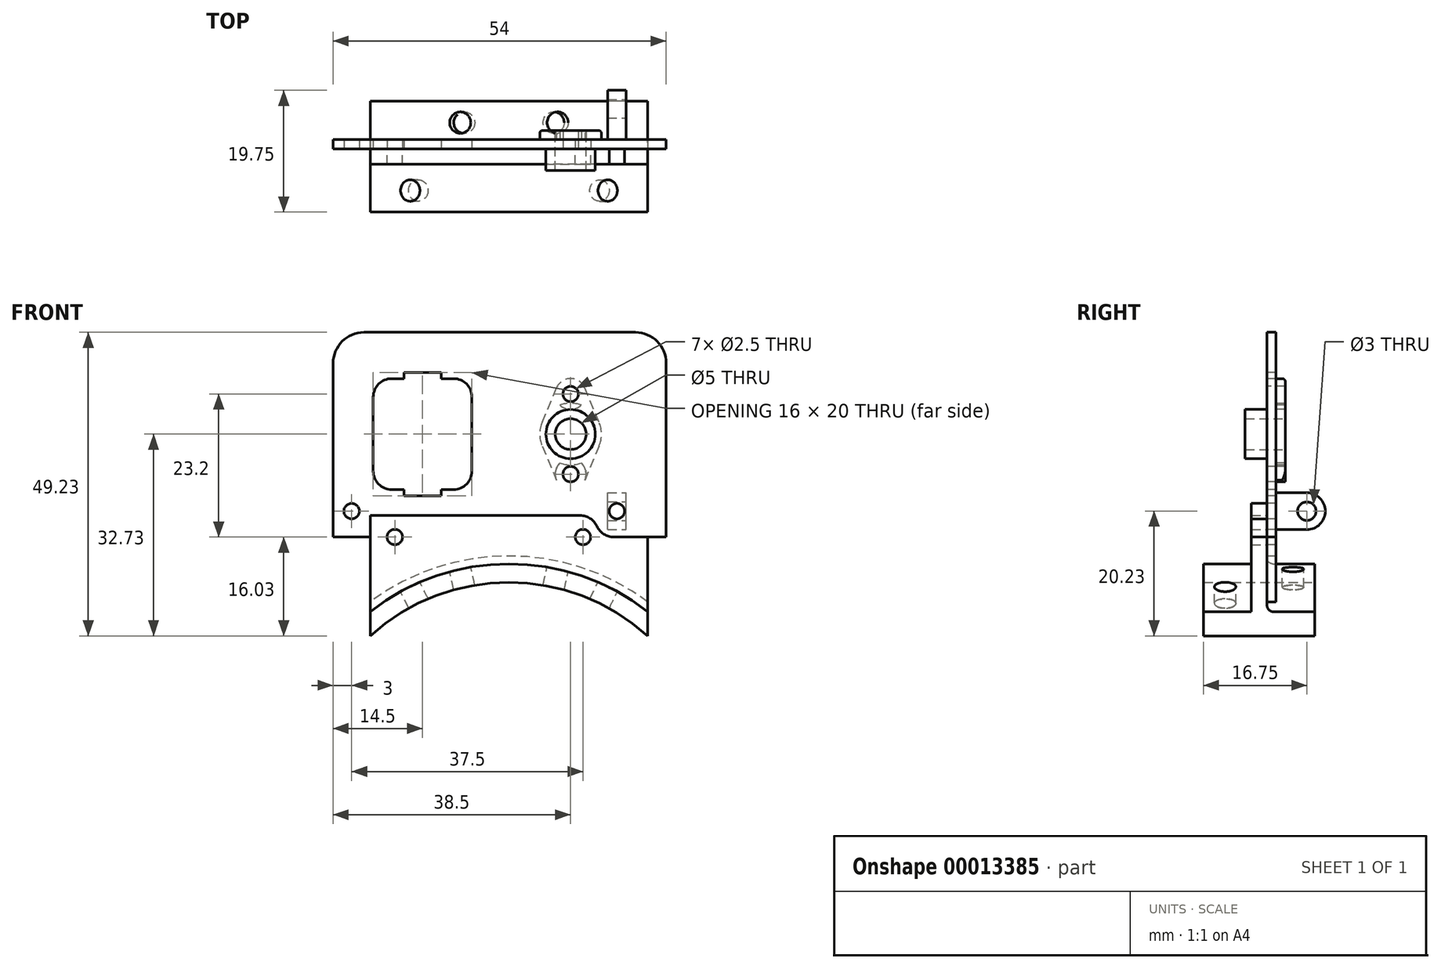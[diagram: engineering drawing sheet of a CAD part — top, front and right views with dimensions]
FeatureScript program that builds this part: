
annotation { "Feature Type Name" : "Feature", "Feature Type Description" : "" }
export const myFeature = defineFeature(function(context is Context, id is Id, definition is map)
    precondition{}
    {
        {
            var Q0;
            Q0=qCreatedBy(makeId("Front.planeOp"),FACE);
            var sketch = newSketch(context, id + "F0", { "sketchPlane" : qUnion([Q0])});
            skCircle(sketch, "E0", {"center": v(0, 0) * mm, "radius": 33.5 * mm});
            skCircle(sketch, "E1", {"center": v(0, 0) * mm, "radius": 36.5 * mm});
            skLineSegment(sketch, "E2", {"start": v(0, 0) * mm, "end": v(0, 40.85) * mm, "construction": true});
            skLineSegment(sketch, "E3", {"start": v(0, 40.85) * mm, "end": v(-22.5, 40.85) * mm, "construction": true});
            skLineSegment(sketch, "E4", {"start": v(0, 40.85) * mm, "end": v(12, 40.85) * mm, "construction": true});
            skCircle(sketch, "E5", {"center": v(-18.5, 40.85) * mm, "radius": 1.25 * mm});
            skCircle(sketch, "E6", {"center": v(12, 40.85) * mm, "radius": 1.25 * mm});
            skLineSegment(sketch, "E7.0", {"start": v(22.5, 0) * mm, "end": v(22.5, 40.85) * mm, "construction": true});
            skLineSegment(sketch, "E8.0.MirrorCS", {"start": v(-22.5, 0) * mm, "end": v(-22.5, 40.85) * mm, "construction": true});
            skLineSegment(sketch, "E9.0", {"start": v(0, 44.35) * mm, "end": v(-22.5, 44.35) * mm});
            skLineSegment(sketch, "E10", {"start": v(-22.5, 44.35) * mm, "end": v(-22.5, 24.82) * mm});
            skLineSegment(sketch, "E11", {"start": v(0, 44.35) * mm, "end": v(22.5, 44.35) * mm});
            skLineSegment(sketch, "E12", {"start": v(22.5, 44.35) * mm, "end": v(22.5, 24.82) * mm});
            skLineSegment(sketch, "E13", {"start": v(22.5, 40.85) * mm, "end": v(17, 40.85) * mm});
            skLineSegment(sketch, "E14.bottom", {"start": v(17, 40.85) * mm, "end": v(12, 40.85) * mm});
            skLineSegment(sketch, "E14.top", {"start": v(17, 44.35) * mm, "end": v(12, 44.35) * mm});
            skLineSegment(sketch, "E14.left", {"start": v(17, 40.85) * mm, "end": v(17, 44.35) * mm});
            skLineSegment(sketch, "E14.right", {"start": v(12, 40.85) * mm, "end": v(12, 44.35) * mm});
            skCircle(sketch, "E15", {"center": v(12, 44.35) * mm, "radius": 3 * mm, "construction": true});
            skCircle(sketch, "E16", {"center": v(17, 40.85) * mm, "radius": 3 * mm, "construction": true});
            skLineSegment(sketch, "E17", {"start": v(12, 41.35) * mm, "end": v(14.04, 41.35) * mm, "construction": true});
            skLineSegment(sketch, "E18", {"start": v(17, 43.85) * mm, "end": v(14.96, 43.85) * mm, "construction": true});
            skCircle(sketch, "E19", {"center": v(17, 43.85) * mm, "radius": 3 * mm});
            skLineSegment(sketch, "E20", {"start": v(12, 41.35) * mm, "end": v(7.9, 41.35) * mm, "construction": true});
            skCircle(sketch, "E21", {"center": v(17, 43.85) * mm, "radius": 6 * mm, "construction": true});
            skCircle(sketch, "E22", {"center": v(11.55, 41.35) * mm, "radius": 3 * mm});
            skSolve(sketch);
        }
        {
            var Q0;
            {var subQ3=sQuery(id+"F0.wireOp",EDGE,"E0");var subQ5=sQuery(id+"F0.wireOp",EDGE,"E10");var subQ7=makeQuery(id+"F0.imprint","INTERSECT",VERTEX,{"derivedFrom":[subQ3,subQ5]});Q0=makeQuery(id+"F0.imprint","IMPRINT",FACE,{"disambiguationData":[TD([[makeQuery(id+"F0.imprint","IMPRINT",EDGE,{"disambiguationData":[TD([[subQ7,1.0]])],"derivedFrom":subQ3}),-1.0]])]});}
            extrude(context, id + "F1", {"entities" : qUnion([Q0]), "endBound" : BoundingType.SYMMETRIC, "depth" : 18 * mm});
        }
        {
            var Q0;
            Q0=makeQuery(id+"F0.imprint","IMPRINT",FACE,{"disambiguationData":[TD([[makeQuery(id+"F0.imprint","IMPRINT",EDGE,{"derivedFrom":sQuery(id+"F0.wireOp",EDGE,"E5")}),-1.0]])]});
            var Q1;
            {var subQ1=sQuery(id+"F0.wireOp",EDGE,"E14.bottom");var subQ6=sQuery(id+"F0.wireOp",EDGE,"E6");var subQ8=makeQuery(id+"F0.imprint","INTERSECT",VERTEX,{"derivedFrom":[subQ6,subQ1]});Q1=makeQuery(id+"F0.imprint","IMPRINT",FACE,{"disambiguationData":[TD([[makeQuery(id+"F0.imprint","IMPRINT",EDGE,{"disambiguationData":[TD([[subQ8,1.0]])],"derivedFrom":subQ6}),-1.0]])]});}
            var Q2;
            {var subQ0=sQuery(id+"F0.wireOp",EDGE,"E22");var subQ3=sQuery(id+"F0.wireOp",EDGE,"E14.bottom");var subQ4=makeQuery(id+"F0.imprint","INTERSECT",VERTEX,{"derivedFrom":[subQ3,subQ0]});Q2=makeQuery(id+"F0.imprint","IMPRINT",FACE,{"disambiguationData":[TD([[makeQuery(id+"F0.imprint","IMPRINT",EDGE,{"disambiguationData":[TD([[subQ4,-1.0]])],"derivedFrom":subQ0}),-1.0]])]});}
            var Q3;
            {var subQ2=sQuery(id+"F0.wireOp",EDGE,"E14.bottom");var subQ6=sQuery(id+"F0.wireOp",EDGE,"E6");var subQ8=makeQuery(id+"F0.imprint","INTERSECT",VERTEX,{"derivedFrom":[subQ6,subQ2]});Q3=makeQuery(id+"F0.imprint","IMPRINT",FACE,{"disambiguationData":[TD([[makeQuery(id+"F0.imprint","IMPRINT",EDGE,{"disambiguationData":[TD([[subQ8,-1.0]])],"derivedFrom":subQ6}),-1.0]])]});}
            extrude(context, id + "F2", {"entities" : qUnion([Q0, Q1, Q2, Q3]), "operationType" : NewBodyOperationType.ADD, "endBound" : BoundingType.SYMMETRIC, "depth" : 2.5 * mm});
        }
        {
            var Q0;
            Q0=makeQuery(id+"F2.opExtrude","CAP_FACE",FACE,{"disambiguationData":[OSD([sQuery(id+"F0.wireOp",EDGE,"E1"),sQuery(id+"F0.wireOp",EDGE,"E5"),sQuery(id+"F0.wireOp",EDGE,"E6"),sQuery(id+"F0.wireOp",EDGE,"E10"),sQuery(id+"F0.wireOp",EDGE,"E11"),sQuery(id+"F0.wireOp",EDGE,"E12"),sQuery(id+"F0.wireOp",EDGE,"E13"),sQuery(id+"F0.wireOp",EDGE,"E19"),sQuery(id+"F0.wireOp",EDGE,"E22")])],"isStart":true});
            var sketch = newSketch(context, id + "F3", { "sketchPlane" : qUnion([Q0])});
            skLineSegment(sketch, "E23.0", {"start": v(0, 0) * mm, "end": v(0, 40.85) * mm, "construction": true});
            skCircle(sketch, "E23.1", {"center": v(-12, 40.85) * mm, "radius": 1.25 * mm});
            skCircle(sketch, "E23.2", {"center": v(18.5, 40.85) * mm, "radius": 1.25 * mm});
            skLineSegment(sketch, "E24", {"start": v(0, 40.85) * mm, "end": v(-22.5, 40.85) * mm, "construction": true});
            skLineSegment(sketch, "E25", {"start": v(0, 40.85) * mm, "end": v(22.5, 40.85) * mm, "construction": true});
            skLineSegment(sketch, "E26", {"start": v(-22.5, 40.85) * mm, "end": v(-22.5, 30.35) * mm});
            skLineSegment(sketch, "E27", {"start": v(-22.5, 30.35) * mm, "end": v(22.5, 30.35) * mm});
            skLineSegment(sketch, "E28", {"start": v(22.5, 30.35) * mm, "end": v(22.5, 40.85) * mm});
            skCircle(sketch, "E29", {"center": v(0, 0) * mm, "radius": 37.78 * mm});
            skLineSegment(sketch, "E30.bottom", {"start": v(-22.5, 40.85) * mm, "end": v(-25.5, 40.85) * mm});
            skLineSegment(sketch, "E30.top", {"start": v(-20.5, 74.05) * mm, "end": v(-22.5, 74.05) * mm});
            skLineSegment(sketch, "E30.left", {"start": v(-22.5, 40.85) * mm, "end": v(-22.5, 74.05) * mm});
            skLineSegment(sketch, "E30.right", {"start": v(-25.5, 40.85) * mm, "end": v(-25.5, 69.05) * mm});
            skLineSegment(sketch, "E31.bottom", {"start": v(22.5, 40.85) * mm, "end": v(28.5, 40.85) * mm});
            skLineSegment(sketch, "E31.top", {"start": v(22.5, 74.05) * mm, "end": v(23.5, 74.05) * mm});
            skLineSegment(sketch, "E31.left", {"start": v(22.5, 40.85) * mm, "end": v(22.5, 74.05) * mm});
            skLineSegment(sketch, "E31.right", {"start": v(28.5, 40.85) * mm, "end": v(28.5, 69.05) * mm});
            skLineSegment(sketch, "E32", {"start": v(-22.5, 74.05) * mm, "end": v(22.5, 74.05) * mm});
            skPoint(sketch, "E33.visualSharp", {"position": v(-25.5, 74.05) * mm});
            skArc(sketch, "E33.filletArc", {"start": v(-20.5, 74.05) * mm, "mid": v(-24.04, 72.59) * mm, "end": v(-25.5, 69.05) * mm});
            skPoint(sketch, "E34.visualSharp", {"position": v(28.5, 74.05) * mm});
            skArc(sketch, "E34.filletArc", {"start": v(28.5, 69.05) * mm, "mid": v(27.04, 72.59) * mm, "end": v(23.5, 74.05) * mm});
            skLineSegment(sketch, "E35", {"start": v(0, 40.85) * mm, "end": v(0, 74.05) * mm, "construction": true});
            skLineSegment(sketch, "E36", {"start": v(-10, 74.05) * mm, "end": v(-10, 40.85) * mm, "construction": true});
            skLineSegment(sketch, "E37", {"start": v(14, 74.05) * mm, "end": v(14, 40.85) * mm, "construction": true});
            skLineSegment(sketch, "E38", {"start": v(-17.5, 74.05) * mm, "end": v(-17.5, 45.05) * mm, "construction": true});
            skLineSegment(sketch, "E39", {"start": v(-17.5, 45.05) * mm, "end": v(25.5, 45.05) * mm, "construction": true});
            skLineSegment(sketch, "E40", {"start": v(-25.5, 57.55) * mm, "end": v(28.5, 57.55) * mm, "construction": true});
            skCircle(sketch, "E41", {"center": v(-10, 57.55) * mm, "radius": 4 * mm});
            skCircle(sketch, "E42", {"center": v(-10, 57.55) * mm, "radius": 6.5 * mm, "construction": true});
            skCircle(sketch, "E43", {"center": v(-17.5, 45.05) * mm, "radius": 1.25 * mm});
            skCircle(sketch, "E44", {"center": v(25.5, 45.05) * mm, "radius": 1.25 * mm});
            skLineSegment(sketch, "E45.rect.bottom", {"start": v(17, 47.55) * mm, "end": v(11, 47.55) * mm});
            skLineSegment(sketch, "E45.rect.top", {"start": v(17, 67.55) * mm, "end": v(11, 67.55) * mm});
            skLineSegment(sketch, "E45.rect.left", {"start": v(17, 47.55) * mm, "end": v(17, 67.55) * mm});
            skLineSegment(sketch, "E45.rect.right", {"start": v(11, 47.55) * mm, "end": v(11, 67.55) * mm});
            skPoint(sketch, "E45.rect.middle", {"position": v(14, 57.55) * mm});
            skLineSegment(sketch, "E46.rect.bottom", {"start": v(19, 48.55) * mm, "end": v(9, 48.55) * mm});
            skLineSegment(sketch, "E46.rect.top", {"start": v(19, 66.55) * mm, "end": v(9, 66.55) * mm});
            skLineSegment(sketch, "E46.rect.left", {"start": v(22, 51.55) * mm, "end": v(22, 63.55) * mm});
            skLineSegment(sketch, "E46.rect.right", {"start": v(6, 51.55) * mm, "end": v(6, 63.55) * mm});
            skPoint(sketch, "E47.visualSharp", {"position": v(6, 66.55) * mm});
            skArc(sketch, "E47.filletArc", {"start": v(9, 66.55) * mm, "mid": v(6.88, 65.67) * mm, "end": v(6, 63.55) * mm});
            skPoint(sketch, "E48.visualSharp", {"position": v(6, 48.55) * mm});
            skArc(sketch, "E48.filletArc", {"start": v(6, 51.55) * mm, "mid": v(6.88, 49.43) * mm, "end": v(9, 48.55) * mm});
            skPoint(sketch, "E49.visualSharp", {"position": v(22, 48.55) * mm});
            skArc(sketch, "E49.filletArc", {"start": v(19, 48.55) * mm, "mid": v(21.12, 49.43) * mm, "end": v(22, 51.55) * mm});
            skPoint(sketch, "E50.visualSharp", {"position": v(22, 66.55) * mm});
            skArc(sketch, "E50.filletArc", {"start": v(22, 63.55) * mm, "mid": v(21.12, 65.67) * mm, "end": v(19, 66.55) * mm});
            skCircle(sketch, "E51", {"center": v(-10, 64.05) * mm, "radius": 1.25 * mm});
            skCircle(sketch, "E52.0.MirrorC", {"center": v(-10, 51.05) * mm, "radius": 1.25 * mm});
            skSolve(sketch);
        }
        {
            var Q0;
            Q0=makeQuery(id+"F3.imprint","IMPRINT",FACE,{"disambiguationData":[TD([[makeQuery(id+"F3.imprint","IMPRINT",EDGE,{"derivedFrom":sQuery(id+"F3.wireOp",EDGE,"E23.1")}),1.0]])]});
            var Q1;
            Q1=makeQuery(id+"F3.imprint","IMPRINT",FACE,{"disambiguationData":[TD([[makeQuery(id+"F3.imprint","IMPRINT",EDGE,{"derivedFrom":sQuery(id+"F3.wireOp",EDGE,"E41")}),-1.0]])]});
            var Q2;
            {var subQ4=sQuery(id+"F3.wireOp",EDGE,"E30.bottom");Q2=makeQuery(id+"F3.imprint","IMPRINT",FACE,{"disambiguationData":[TD([[makeQuery(id+"F3.imprint","IMPRINT",EDGE,{"derivedFrom":subQ4}),-1.0]])]});}
            var Q3;
            {var subQ3=sQuery(id+"F3.wireOp",EDGE,"E31.bottom");Q3=makeQuery(id+"F3.imprint","IMPRINT",FACE,{"disambiguationData":[TD([[makeQuery(id+"F3.imprint","IMPRINT",EDGE,{"derivedFrom":subQ3}),1.0]])]});}
            extrude(context, id + "F4", {"entities" : qUnion([Q0, Q1, Q2, Q3]), "depth" : 1.5 * mm});
        }
        {
            var Q0;
            Q0=makeQuery(id+"F2.opExtrude","CAP_EDGE",EDGE,{"disambiguationData":[OSD([sQuery(id+"F0.wireOp",EDGE,"E1")])],"isStart":false});
            var Q1;
            Q1=makeQuery(id+"F2.opExtrude","CAP_EDGE",EDGE,{"disambiguationData":[OSD([sQuery(id+"F0.wireOp",EDGE,"E1")])],"isStart":true});
            fillet(context, id + "F5", {"entities" : qUnion([Q0, Q1]), "radius" : 1 * mm, "tangentPropagation" : true, "allowEdgeOverflow" : false});
        }
        {
            var Q0;
            Q0=makeQuery(id+"F4.opExtrude","CAP_FACE",FACE,{"disambiguationData":[OSD([sQuery(id+"F3.wireOp",EDGE,"E23.1"),sQuery(id+"F3.wireOp",EDGE,"E23.2"),sQuery(id+"F3.wireOp",EDGE,"E26"),sQuery(id+"F3.wireOp",EDGE,"E28"),sQuery(id+"F3.wireOp",EDGE,"E29"),sQuery(id+"F3.wireOp",EDGE,"E30.bottom"),sQuery(id+"F3.wireOp",EDGE,"E30.right"),sQuery(id+"F3.wireOp",EDGE,"E31.bottom"),sQuery(id+"F3.wireOp",EDGE,"E31.top"),sQuery(id+"F3.wireOp",EDGE,"E31.right"),sQuery(id+"F3.wireOp",EDGE,"E32"),sQuery(id+"F3.wireOp",EDGE,"E33.filletArc"),sQuery(id+"F3.wireOp",EDGE,"E34.filletArc"),sQuery(id+"F3.wireOp",EDGE,"E41"),sQuery(id+"F3.wireOp",EDGE,"E43"),sQuery(id+"F3.wireOp",EDGE,"E44"),sQuery(id+"F3.wireOp",EDGE,"E45.rect.bottom"),sQuery(id+"F3.wireOp",EDGE,"E45.rect.top"),sQuery(id+"F3.wireOp",EDGE,"E45.rect.left"),sQuery(id+"F3.wireOp",EDGE,"E45.rect.right"),sQuery(id+"F3.wireOp",EDGE,"E46.rect.bottom"),sQuery(id+"F3.wireOp",EDGE,"E46.rect.top"),sQuery(id+"F3.wireOp",EDGE,"E46.rect.left"),sQuery(id+"F3.wireOp",EDGE,"E46.rect.right"),sQuery(id+"F3.wireOp",EDGE,"E47.filletArc"),sQuery(id+"F3.wireOp",EDGE,"E48.filletArc"),sQuery(id+"F3.wireOp",EDGE,"E49.filletArc"),sQuery(id+"F3.wireOp",EDGE,"E50.filletArc"),sQuery(id+"F3.wireOp",EDGE,"E51"),sQuery(id+"F3.wireOp",EDGE,"E52.0.MirrorC")])],"isStart":false});
            var sketch = newSketch(context, id + "F6", { "sketchPlane" : qUnion([Q0])});
            skCircle(sketch, "E53.0", {"center": v(-10, 57.55) * mm, "radius": 4 * mm});
            skCircle(sketch, "E53.1", {"center": v(-10, 64.05) * mm, "radius": 1.25 * mm});
            skCircle(sketch, "E53.2", {"center": v(-10, 51.05) * mm, "radius": 1.25 * mm});
            skCircle(sketch, "E54", {"center": v(-10, 57.55) * mm, "radius": 5 * mm});
            skCircle(sketch, "E55", {"center": v(-10, 57.55) * mm, "radius": 2.5 * mm});
            skCircle(sketch, "E56", {"center": v(-10, 64.05) * mm, "radius": 2.5 * mm});
            skCircle(sketch, "E57", {"center": v(-10, 51.05) * mm, "radius": 2.5 * mm});
            skLineSegment(sketch, "E58", {"start": v(-14.62, 55.63) * mm, "end": v(-12.3, 50.09) * mm});
            skLineSegment(sketch, "E59", {"start": v(-5.38, 55.63) * mm, "end": v(-7.7, 50.09) * mm});
            skLineSegment(sketch, "E60", {"start": v(-14.62, 59.47) * mm, "end": v(-12.3, 65.01) * mm});
            skLineSegment(sketch, "E61", {"start": v(-5.38, 59.47) * mm, "end": v(-7.7, 65.01) * mm});
            skSolve(sketch);
        }
        {
            var Q0;
            Q0=makeQuery(id+"F6.imprint","IMPRINT",FACE,{"disambiguationData":[TD([[makeQuery(id+"F6.imprint","IMPRINT",EDGE,{"derivedFrom":sQuery(id+"F6.wireOp",EDGE,"E55")}),-1.0]])]});
            extrude(context, id + "F7", {"entities" : qUnion([Q0]), "oppositeDirection" : true, "depth" : 5 * mm});
        }
        {
            var Q0;
            {var subQ3=sQuery(id+"F6.wireOp",EDGE,"E53.0");var subQ5=sQuery(id+"F6.wireOp",EDGE,"E56");var subQ7=makeQuery(id+"F6.imprint","INTERSECT",VERTEX,{"derivedFrom":[subQ3,subQ5]});Q0=makeQuery(id+"F6.imprint","IMPRINT",FACE,{"disambiguationData":[TD([[makeQuery(id+"F6.imprint","IMPRINT",EDGE,{"disambiguationData":[TD([[subQ7,-1.0]])],"derivedFrom":subQ3}),-1.0]])]});}
            var Q1;
            Q1=makeQuery(id+"F6.imprint","IMPRINT",FACE,{"disambiguationData":[TD([[makeQuery(id+"F6.imprint","IMPRINT",EDGE,{"derivedFrom":sQuery(id+"F6.wireOp",EDGE,"E55")}),-1.0]])]});
            var Q2;
            {var subQ0=sQuery(id+"F6.wireOp",EDGE,"E56");var subQ1=sQuery(id+"F6.wireOp",EDGE,"E54");var subQ2=makeQuery(id+"F6.imprint","INTERSECT",VERTEX,{"disambiguationData":[OD(0.0)],"derivedFrom":[subQ1,subQ0]});Q2=makeQuery(id+"F6.imprint","IMPRINT",FACE,{"disambiguationData":[TD([[makeQuery(id+"F6.imprint","IMPRINT",EDGE,{"disambiguationData":[TD([[subQ2,-1.0]])],"derivedFrom":subQ1}),1.0]])]});}
            var Q3;
            Q3=makeQuery(id+"F6.imprint","IMPRINT",FACE,{"disambiguationData":[TD([[makeQuery(id+"F6.imprint","IMPRINT",EDGE,{"derivedFrom":sQuery(id+"F6.wireOp",EDGE,"E53.1")}),-1.0]])]});
            var Q4;
            {var subQ0=sQuery(id+"F6.wireOp",EDGE,"E60");Q4=makeQuery(id+"F6.imprint","IMPRINT",FACE,{"disambiguationData":[TD([[makeQuery(id+"F6.imprint","IMPRINT",EDGE,{"derivedFrom":subQ0}),-1.0]])]});}
            var Q5;
            {var subQ3=sQuery(id+"F6.wireOp",EDGE,"E53.0");var subQ5=sQuery(id+"F6.wireOp",EDGE,"E56");var subQ7=makeQuery(id+"F6.imprint","INTERSECT",VERTEX,{"derivedFrom":[subQ3,subQ5]});Q5=makeQuery(id+"F6.imprint","IMPRINT",FACE,{"disambiguationData":[TD([[makeQuery(id+"F6.imprint","IMPRINT",EDGE,{"disambiguationData":[TD([[subQ7,1.0]])],"derivedFrom":subQ3}),-1.0]])]});}
            var Q6;
            {var subQ0=sQuery(id+"F6.wireOp",EDGE,"E61");Q6=makeQuery(id+"F6.imprint","IMPRINT",FACE,{"disambiguationData":[TD([[makeQuery(id+"F6.imprint","IMPRINT",EDGE,{"derivedFrom":subQ0}),1.0]])]});}
            var Q7;
            {var subQ0=sQuery(id+"F6.wireOp",EDGE,"E57");var subQ1=sQuery(id+"F6.wireOp",EDGE,"E54");var subQ2=makeQuery(id+"F6.imprint","INTERSECT",VERTEX,{"disambiguationData":[OD(0.0)],"derivedFrom":[subQ1,subQ0]});Q7=makeQuery(id+"F6.imprint","IMPRINT",FACE,{"disambiguationData":[TD([[makeQuery(id+"F6.imprint","IMPRINT",EDGE,{"disambiguationData":[TD([[subQ2,-1.0]])],"derivedFrom":subQ1}),1.0]])]});}
            var Q8;
            Q8=makeQuery(id+"F6.imprint","IMPRINT",FACE,{"disambiguationData":[TD([[makeQuery(id+"F6.imprint","IMPRINT",EDGE,{"derivedFrom":sQuery(id+"F6.wireOp",EDGE,"E53.2")}),1.0]])]});
            var Q9;
            {var subQ0=sQuery(id+"F6.wireOp",EDGE,"E58");Q9=makeQuery(id+"F6.imprint","IMPRINT",FACE,{"disambiguationData":[TD([[makeQuery(id+"F6.imprint","IMPRINT",EDGE,{"derivedFrom":subQ0}),1.0]])]});}
            var Q10;
            {var subQ0=sQuery(id+"F6.wireOp",EDGE,"E59");Q10=makeQuery(id+"F6.imprint","IMPRINT",FACE,{"disambiguationData":[TD([[makeQuery(id+"F6.imprint","IMPRINT",EDGE,{"derivedFrom":subQ0}),-1.0]])]});}
            extrude(context, id + "F8", {"entities" : qUnion([Q0, Q1, Q2, Q3, Q4, Q5, Q6, Q7, Q8, Q9, Q10]), "operationType" : NewBodyOperationType.ADD, "depth" : 1.5 * mm});
        }
        {
            var Q0;
            Q0=makeQuery(id+"F8.opExtrude","CAP_EDGE",EDGE,{"disambiguationData":[OSD([sQuery(id+"F6.wireOp",EDGE,"E60")])],"isStart":false});
            fillet(context, id + "F9", {"entities" : qUnion([Q0]), "radius" : 0.5 * mm, "tangentPropagation" : true, "allowEdgeOverflow" : false});
        }
        {
            var Q0;
            Q0=makeQuery(id+"F4.opExtrude","CAP_FACE",FACE,{"disambiguationData":[OSD([sQuery(id+"F3.wireOp",EDGE,"E23.1"),sQuery(id+"F3.wireOp",EDGE,"E23.2"),sQuery(id+"F3.wireOp",EDGE,"E26"),sQuery(id+"F3.wireOp",EDGE,"E28"),sQuery(id+"F3.wireOp",EDGE,"E29"),sQuery(id+"F3.wireOp",EDGE,"E30.bottom"),sQuery(id+"F3.wireOp",EDGE,"E30.right"),sQuery(id+"F3.wireOp",EDGE,"E31.bottom"),sQuery(id+"F3.wireOp",EDGE,"E31.top"),sQuery(id+"F3.wireOp",EDGE,"E31.right"),sQuery(id+"F3.wireOp",EDGE,"E32"),sQuery(id+"F3.wireOp",EDGE,"E33.filletArc"),sQuery(id+"F3.wireOp",EDGE,"E34.filletArc"),sQuery(id+"F3.wireOp",EDGE,"E41"),sQuery(id+"F3.wireOp",EDGE,"E43"),sQuery(id+"F3.wireOp",EDGE,"E44"),sQuery(id+"F3.wireOp",EDGE,"E45.rect.bottom"),sQuery(id+"F3.wireOp",EDGE,"E45.rect.top"),sQuery(id+"F3.wireOp",EDGE,"E45.rect.left"),sQuery(id+"F3.wireOp",EDGE,"E45.rect.right"),sQuery(id+"F3.wireOp",EDGE,"E46.rect.bottom"),sQuery(id+"F3.wireOp",EDGE,"E46.rect.top"),sQuery(id+"F3.wireOp",EDGE,"E46.rect.left"),sQuery(id+"F3.wireOp",EDGE,"E46.rect.right"),sQuery(id+"F3.wireOp",EDGE,"E47.filletArc"),sQuery(id+"F3.wireOp",EDGE,"E48.filletArc"),sQuery(id+"F3.wireOp",EDGE,"E49.filletArc"),sQuery(id+"F3.wireOp",EDGE,"E50.filletArc"),sQuery(id+"F3.wireOp",EDGE,"E51"),sQuery(id+"F3.wireOp",EDGE,"E52.0.MirrorC")])],"isStart":false});
            var sketch = newSketch(context, id + "F10", { "sketchPlane" : qUnion([Q0])});
            skCircle(sketch, "E62.0", {"center": v(-17.5, 45.05) * mm, "radius": 1.25 * mm});
            skLineSegment(sketch, "E63.rect.bottom", {"start": v(-16, 42.05) * mm, "end": v(-19, 42.05) * mm});
            skLineSegment(sketch, "E63.rect.top", {"start": v(-16, 48.05) * mm, "end": v(-19, 48.05) * mm});
            skLineSegment(sketch, "E63.rect.left", {"start": v(-16, 42.05) * mm, "end": v(-16, 48.05) * mm});
            skLineSegment(sketch, "E63.rect.right", {"start": v(-19, 42.05) * mm, "end": v(-19, 48.05) * mm});
            skSolve(sketch);
        }
        {
            var Q0;
            Q0=makeQuery(id+"F10.imprint","IMPRINT",FACE,{"disambiguationData":[TD([[makeQuery(id+"F10.imprint","IMPRINT",EDGE,{"derivedFrom":sQuery(id+"F10.wireOp",EDGE,"E62.0")}),1.0]])]});
            extrude(context, id + "F11", {"entities" : qUnion([Q0]), "oppositeDirection" : true, "depth" : 4 * mm});
        }
        {
            var Q0;
            Q0=makeQuery(id+"F10.imprint","IMPRINT",FACE,{"disambiguationData":[TD([[makeQuery(id+"F10.imprint","IMPRINT",EDGE,{"derivedFrom":sQuery(id+"F10.wireOp",EDGE,"E62.0")}),-1.0]])]});
            var Q1;
            Q1=makeQuery(id+"F10.imprint","IMPRINT",FACE,{"disambiguationData":[TD([[makeQuery(id+"F10.imprint","IMPRINT",EDGE,{"derivedFrom":sQuery(id+"F10.wireOp",EDGE,"E62.0")}),1.0]])]});
            extrude(context, id + "F12", {"entities" : qUnion([Q0, Q1]), "operationType" : NewBodyOperationType.ADD, "depth" : 8 * mm});
        }
        {
            var Q0;
            Q0=makeQuery(id+"F12.opExtrude","SWEPT_FACE",FACE,{"disambiguationData":[OSD([sQuery(id+"F10.wireOp",EDGE,"E63.rect.right")])]});
            var sketch = newSketch(context, id + "F13", { "sketchPlane" : qUnion([Q0])});
            skLineSegment(sketch, "E64", {"start": v(10.75, 45.05) * mm, "end": v(7.75, 45.05) * mm, "construction": true});
            skCircle(sketch, "E65", {"center": v(7.75, 45.05) * mm, "radius": 3 * mm});
            skCircle(sketch, "E66", {"center": v(7.75, 45.05) * mm, "radius": 1.5 * mm});
            skSolve(sketch);
        }
        {
            var Q0;
            Q0=makeQuery(id+"F13.imprint","IMPRINT",FACE,{"disambiguationData":[TD([[makeQuery(id+"F13.imprint","IMPRINT",EDGE,{"derivedFrom":sQuery(id+"F13.wireOp",EDGE,"E66")}),1.0]])]});
            var Q1;
            {var subQ0=sQuery(id+"F10.wireOp",EDGE,"E63.rect.right");var subQ1=makeQuery(id+"F12.opExtrude","CAP_EDGE",EDGE,{"disambiguationData":[OSD([subQ0])],"isStart":false});var subQ2=sQuery(id+"F13.wireOp",EDGE,"E65");var subQ3=makeQuery(id+"F13.imprint","INTERSECT",VERTEX,{"derivedFrom":[subQ1,subQ2]});Q1=makeQuery(id+"F13.imprint","IMPRINT",FACE,{"disambiguationData":[TD([[makeQuery(id+"F13.imprint","IMPRINT",EDGE,{"disambiguationData":[TD([[subQ3,-1.0]])],"derivedFrom":subQ2}),-1.0]])]});}
            var Q2;
            {var subQ0=sQuery(id+"F10.wireOp",EDGE,"E63.rect.right");var subQ1=makeQuery(id+"F12.opExtrude","CAP_EDGE",EDGE,{"disambiguationData":[OSD([subQ0])],"isStart":false});var subQ2=sQuery(id+"F13.wireOp",EDGE,"E65");var subQ3=makeQuery(id+"F13.imprint","INTERSECT",VERTEX,{"derivedFrom":[subQ1,subQ2]});Q2=makeQuery(id+"F13.imprint","IMPRINT",FACE,{"disambiguationData":[TD([[makeQuery(id+"F13.imprint","IMPRINT",EDGE,{"disambiguationData":[TD([[subQ3,1.0]])],"derivedFrom":subQ2}),-1.0]])]});}
            extrude(context, id + "F14", {"entities" : qUnion([Q0, Q1, Q2]), "operationType" : NewBodyOperationType.REMOVE, "oppositeDirection" : true, "depth" : 3 * mm});
        }
        {
            var Q0;
            Q0=qCreatedBy(makeId("Front.planeOp"),FACE);
            cPlane(context, id + "F15", {"entities" : qUnion([Q0]), "cplaneType" : CPlaneType.OFFSET, "offset" : 5.5 * mm, "width" : 150 * mm, "height" : 150 * mm});
        }
        {
            var Q0;
            Q0=qCreatedBy(id+"F15.planeOp",FACE);
            var sketch = newSketch(context, id + "F16", { "sketchPlane" : qUnion([Q0])});
            skCircle(sketch, "E67.0", {"center": v(0, 0) * mm, "radius": 33.5 * mm, "construction": true});
            skCircle(sketch, "E67.1", {"center": v(0, 0) * mm, "radius": 36.5 * mm, "construction": true});
            skLineSegment(sketch, "E68", {"start": v(0, 0) * mm, "end": v(0, 36.5) * mm, "construction": true});
            skLineSegment(sketch, "E69.0", {"start": v(14.7, 0) * mm, "end": v(14.7, 36.5) * mm, "construction": true});
            skLineSegment(sketch, "E70", {"start": v(0, 0) * mm, "end": v(14.7, 30.1) * mm, "construction": true});
            skLineSegment(sketch, "E71", {"start": v(14.7, 30.1) * mm, "end": v(16.46, 33.71) * mm});
            skLineSegment(sketch, "E72", {"start": v(16.46, 33.71) * mm, "end": v(18.03, 32.94) * mm});
            skLineSegment(sketch, "E73", {"start": v(18.03, 32.94) * mm, "end": v(15.55, 27.86) * mm});
            skLineSegment(sketch, "E74", {"start": v(15.55, 27.86) * mm, "end": v(13.98, 28.63) * mm});
            skLineSegment(sketch, "E75", {"start": v(13.98, 28.63) * mm, "end": v(14.7, 30.1) * mm});
            skLineSegment(sketch, "E76.0.MirrorCS", {"start": v(-14.7, 30.1) * mm, "end": v(-16.46, 33.71) * mm});
            skLineSegment(sketch, "E77.0.MirrorCS", {"start": v(-16.46, 33.71) * mm, "end": v(-18.03, 32.94) * mm});
            skLineSegment(sketch, "E78.0.MirrorCS", {"start": v(-18.03, 32.94) * mm, "end": v(-15.55, 27.86) * mm});
            skLineSegment(sketch, "E79.0.MirrorCS", {"start": v(-15.55, 27.86) * mm, "end": v(-13.98, 28.63) * mm});
            skLineSegment(sketch, "E80.0.MirrorCS", {"start": v(-13.98, 28.63) * mm, "end": v(-14.7, 30.1) * mm});
            skSolve(sketch);
        }
        {
            var Q0;
            Q0=makeQuery(id+"F16.imprint","IMPRINT",FACE,{"disambiguationData":[TD([[makeQuery(id+"F16.imprint","IMPRINT",EDGE,{"derivedFrom":sQuery(id+"F16.wireOp",EDGE,"E76.0.MirrorCS")}),1.0]])]});
            var Q1;
            Q1=sQuery(id+"F16.wireOp",EDGE,"E76.0.MirrorCS");
            revolve(context, id + "F17", {"operationType" : NewBodyOperationType.REMOVE, "entities" : qUnion([Q0]), "axis" : qUnion([Q1]), "revolveType" : RevolveType.FULL, "oppositeDirection" : true});
        }
        {
            var Q0;
            Q0=makeQuery(id+"F16.imprint","IMPRINT",FACE,{"disambiguationData":[TD([[makeQuery(id+"F16.imprint","IMPRINT",EDGE,{"derivedFrom":sQuery(id+"F16.wireOp",EDGE,"E71")}),-1.0]])]});
            var Q1;
            Q1=sQuery(id+"F16.wireOp",EDGE,"E75");
            revolve(context, id + "F18", {"operationType" : NewBodyOperationType.REMOVE, "entities" : qUnion([Q0]), "axis" : qUnion([Q1]), "revolveType" : RevolveType.FULL, "oppositeDirection" : true});
        }
        {
            var Q0;
            Q0=qCreatedBy(makeId("Front.planeOp"),FACE);
            cPlane(context, id + "F19", {"entities" : qUnion([Q0]), "cplaneType" : CPlaneType.OFFSET, "offset" : 5.5 * mm, "oppositeDirection" : true, "width" : 150 * mm, "height" : 150 * mm});
        }
        {
            var Q0;
            Q0=qCreatedBy(id+"F19.planeOp",FACE);
            var sketch = newSketch(context, id + "F20", { "sketchPlane" : qUnion([Q0])});
            skCircle(sketch, "E81.0", {"center": v(0, 0) * mm, "radius": 36.5 * mm, "construction": true});
            skCircle(sketch, "E81.1", {"center": v(0, 0) * mm, "radius": 33.5 * mm, "construction": true});
            skLineSegment(sketch, "E81.2", {"start": v(0, 0) * mm, "end": v(0, 36.5) * mm, "construction": true});
            skLineSegment(sketch, "E82.0", {"start": v(7.25, 0) * mm, "end": v(7.25, 36.5) * mm, "construction": true});
            skLineSegment(sketch, "E83", {"start": v(0, 0) * mm, "end": v(7.25, 32.7) * mm, "construction": true});
            skLineSegment(sketch, "E84", {"start": v(7.25, 32.7) * mm, "end": v(7.95, 35.87) * mm});
            skLineSegment(sketch, "E85", {"start": v(7.95, 35.87) * mm, "end": v(9.66, 35.49) * mm});
            skLineSegment(sketch, "E86", {"start": v(9.66, 35.49) * mm, "end": v(8.74, 31.34) * mm});
            skLineSegment(sketch, "E87", {"start": v(8.74, 31.34) * mm, "end": v(7.03, 31.72) * mm});
            skLineSegment(sketch, "E88", {"start": v(7.03, 31.72) * mm, "end": v(7.25, 32.7) * mm});
            skLineSegment(sketch, "E89.0.MirrorCS", {"start": v(-8.74, 31.34) * mm, "end": v(-7.03, 31.72) * mm});
            skLineSegment(sketch, "E90.0.MirrorCS", {"start": v(-7.03, 31.72) * mm, "end": v(-7.25, 32.7) * mm});
            skLineSegment(sketch, "E91.0.MirrorCS", {"start": v(-7.25, 32.7) * mm, "end": v(-7.95, 35.87) * mm});
            skLineSegment(sketch, "E92.0.MirrorCS", {"start": v(-7.95, 35.87) * mm, "end": v(-9.66, 35.49) * mm});
            skLineSegment(sketch, "E93.0.MirrorCS", {"start": v(-9.66, 35.49) * mm, "end": v(-8.74, 31.34) * mm});
            skSolve(sketch);
        }
        {
            var Q0;
            Q0=makeQuery(id+"F20.imprint","IMPRINT",FACE,{"disambiguationData":[TD([[makeQuery(id+"F20.imprint","IMPRINT",EDGE,{"derivedFrom":sQuery(id+"F20.wireOp",EDGE,"E89.0.MirrorCS")}),1.0]])]});
            var Q1;
            Q1=sQuery(id+"F20.wireOp",EDGE,"E91.0.MirrorCS");
            revolve(context, id + "F21", {"operationType" : NewBodyOperationType.REMOVE, "entities" : qUnion([Q0]), "axis" : qUnion([Q1]), "revolveType" : RevolveType.FULL, "oppositeDirection" : true});
        }
        {
            var Q0;
            Q0=makeQuery(id+"F20.imprint","IMPRINT",FACE,{"disambiguationData":[TD([[makeQuery(id+"F20.imprint","IMPRINT",EDGE,{"derivedFrom":sQuery(id+"F20.wireOp",EDGE,"E84")}),-1.0]])]});
            var Q1;
            Q1=sQuery(id+"F20.wireOp",EDGE,"E84");
            revolve(context, id + "F22", {"operationType" : NewBodyOperationType.REMOVE, "entities" : qUnion([Q0]), "axis" : qUnion([Q1]), "revolveType" : RevolveType.FULL, "oppositeDirection" : true});
        }
    });
